# Revit family: Specialty_Equipment-Fiberstone_Planter-Stone_Yard-Concava-Square-Rectangular
name_source: partatom
category: Specialty Equipment
units: mm (PartAtom-declared; Revit-internal decimal feet)

## family parameters
Always vertical = Yes
Cut with Voids When Loaded = No
Enable Cutting in Views = No
Maintain Annotation Orientation = No
OmniClass Number = 23.40.05.21.17
OmniClass Title = Planters
Part Type = Normal
Room Calculation Point = No
Round Connector Dimension = Use Diameter
Shared = No
Work Plane-Based = No

## types (6) — shared parameters
Assembly Code = G2050600
CD_Finish = Concrete-Fiberstone-Carlsbad-Chalk
CD_Microsite = https://www.caddetails.com
CD_Product Page URL = https://stoneyardinc.com
CD_Specification = https://stoneyardinc.com
Default Elevation = 0.0"
Manufacturer = Stone Yard
Model = Concava Planter
URL = https://stoneyardinc.com

## per-type parameters (varying)
| type | CD_Height | CD_Length | CD_Width | Description | Type Comments |
| 48"L x 16"W x 18"H | 18.0" | 48.0" | 16.0" | Concava Rectangular Planter | Rectangular Planter |
| 48"L x 16"W x 22"H | 22.0" | 48.0" | 16.0" | Concava Rectangular Planter | Rectangular Planter |
| 64"L x 16"W x 18"H | 18.0" | 64.0" | 16.0" | Concava Rectangular Planter | Rectangular Planter |
| 64"L x 16"W x 22"H | 22.0" | 64.0" | 16.0" | Concava Rectangular Planter | Rectangular Planter |
| 24"Sq x 22"H | 22.0" | 24.0" | 24.0" | Concava Square Planter | Square Planter |
| 32"Sq x 31"H | 31.0" | 32.0" | 32.0" | Concava Square Planter | Square Planter |

## geometry (parser evidence)
native form markers: Sweep x2
no freeform markers — native parametric forms only
